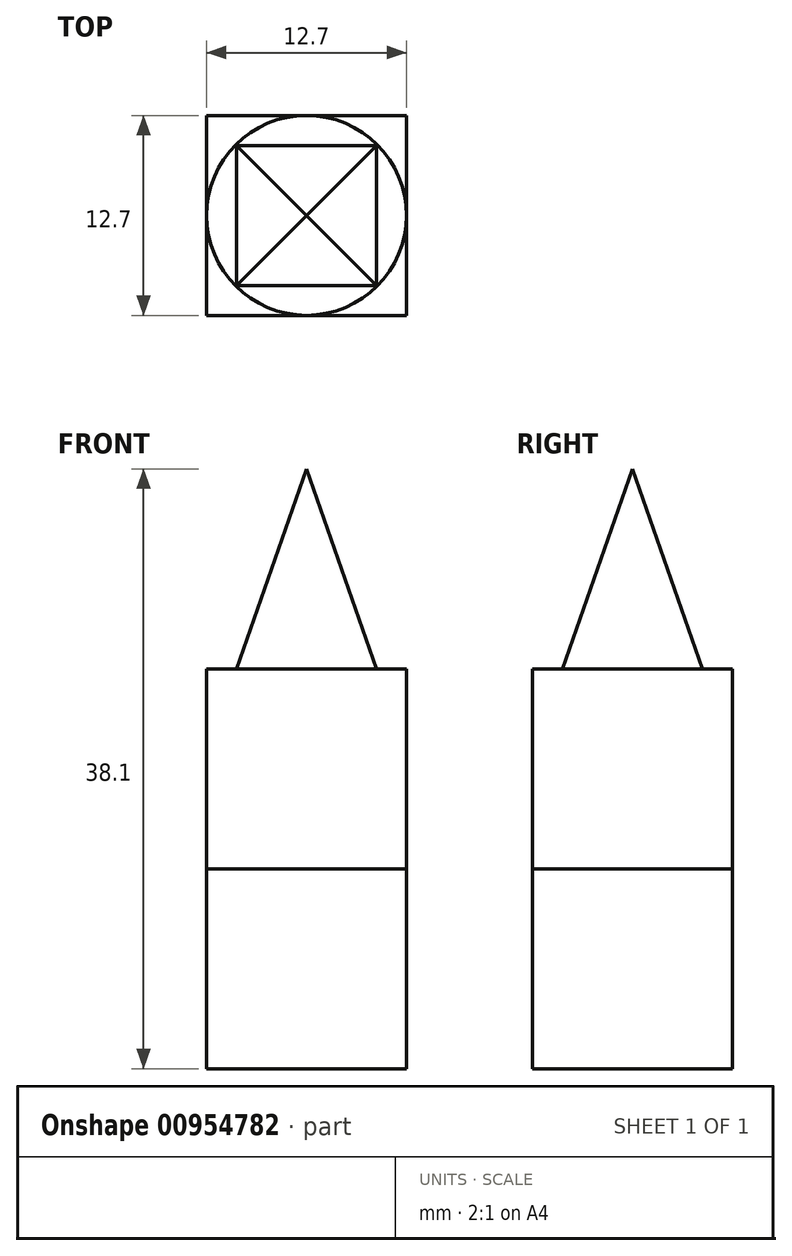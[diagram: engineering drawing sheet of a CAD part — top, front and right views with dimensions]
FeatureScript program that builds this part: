
annotation { "Feature Type Name" : "Feature", "Feature Type Description" : "" }
export const myFeature = defineFeature(function(context is Context, id is Id, definition is map)
    precondition{}
    {
        {
            var Q0;
            Q0=qCreatedBy(makeId("Top.planeOp"),FACE);
            var sketch = newSketch(context, id + "F0", { "sketchPlane" : qUnion([Q0])});
            skLineSegment(sketch, "E0.bottom", {"start": v(6.35, 6.35) * mm, "end": v(-6.35, 6.35) * mm});
            skLineSegment(sketch, "E0.top", {"start": v(6.35, -6.35) * mm, "end": v(-6.35, -6.35) * mm});
            skLineSegment(sketch, "E0.left", {"start": v(6.35, 6.35) * mm, "end": v(6.35, -6.35) * mm});
            skLineSegment(sketch, "E0.right", {"start": v(-6.35, 6.35) * mm, "end": v(-6.35, -6.35) * mm});
            skPoint(sketch, "E0.middle", {"position": v(0, 0) * mm});
            skSolve(sketch);
        }
        {
            var Q0;
            Q0 = qSketchRegion(id + "F0", true);
            extrude(context, id + "F1", {"entities" : qUnion([Q0]), "depth" : 12.7 * mm, "offsetDistance" : 25.4 * mm});
        }
        {
            var Q0;
            Q0=makeQuery(id+"F1.opExtrude","CAP_FACE",FACE,{"disambiguationData":[OSD([sQuery(id+"F0.wireOp",EDGE,"E0.bottom"),sQuery(id+"F0.wireOp",EDGE,"E0.top"),sQuery(id+"F0.wireOp",EDGE,"E0.left"),sQuery(id+"F0.wireOp",EDGE,"E0.right")])],"isStart":false});
            var sketch = newSketch(context, id + "F2", { "sketchPlane" : qUnion([Q0])});
            skCircle(sketch, "E1", {"center": v(0, 0) * mm, "radius": 6.35 * mm});
            skSolve(sketch);
        }
        {
            var Q0;
            Q0 = qSketchRegion(id + "F2", true);
            extrude(context, id + "F3", {"entities" : qUnion([Q0]), "operationType" : NewBodyOperationType.ADD, "depth" : 12.7 * mm, "offsetDistance" : 25.4 * mm});
        }
        {
            var Q0;
            Q0=makeQuery(id+"F3.opExtrude","CAP_FACE",FACE,{"disambiguationData":[OSD([sQuery(id+"F2.wireOp",EDGE,"E1")])],"isStart":false});
            var sketch = newSketch(context, id + "F4", { "sketchPlane" : qUnion([Q0])});
            skLineSegment(sketch, "E2.bottom", {"start": v(6.35, 6.35) * mm, "end": v(-6.35, 6.35) * mm});
            skLineSegment(sketch, "E2.top", {"start": v(6.35, -6.35) * mm, "end": v(-6.35, -6.35) * mm});
            skLineSegment(sketch, "E2.left", {"start": v(6.35, 6.35) * mm, "end": v(6.35, -6.35) * mm});
            skLineSegment(sketch, "E2.right", {"start": v(-6.35, 6.35) * mm, "end": v(-6.35, -6.35) * mm});
            skPoint(sketch, "E2.middle", {"position": v(0, 0) * mm});
            skSolve(sketch);
        }
        {
            var Q0;
            Q0 = qSketchRegion(id + "F4", true);
            extrude(context, id + "F5", {"entities" : qUnion([Q0]), "operationType" : NewBodyOperationType.ADD, "depth" : 12.7 * mm, "offsetDistance" : 25.4 * mm});
        }
        {
            var Q0;
            Q0=qCreatedBy(makeId("Front.planeOp"),FACE);
            var sketch = newSketch(context, id + "F6", { "sketchPlane" : qUnion([Q0])});
            skLineSegment(sketch, "E3.0", {"start": v(6.35, 25.4) * mm, "end": v(4.44, 25.4) * mm});
            skLineSegment(sketch, "E4.0", {"start": v(-4.44, 25.4) * mm, "end": v(-6.35, 25.4) * mm});
            skLineSegment(sketch, "E5.0", {"start": v(6.35, 38.1) * mm, "end": v(-6.35, 38.1) * mm});
            skLineSegment(sketch, "E6", {"start": v(-4.45, 25.4) * mm, "end": v(0, 38.1) * mm});
            skLineSegment(sketch, "E7", {"start": v(0, 38.1) * mm, "end": v(4.44, 25.4) * mm});
            skPoint(sketch, "E8.orphan", {"position": v(0, 25.4) * mm});
            skLineSegment(sketch, "E9.0", {"start": v(-6.35, 38.1) * mm, "end": v(-6.35, 25.4) * mm});
            skLineSegment(sketch, "E10.0", {"start": v(6.35, 38.1) * mm, "end": v(6.35, 25.4) * mm});
            skSolve(sketch);
        }
        {
            var Q0;
            Q0 = qSketchRegion(id + "F6", true);
            extrude(context, id + "F7", {"entities" : qUnion([Q0]), "operationType" : NewBodyOperationType.REMOVE, "endBound" : BoundingType.THROUGH_ALL, "oppositeDirection" : true, "depth" : 25.4 * mm, "offsetDistance" : 25.4 * mm, "hasSecondDirection" : true, "secondDirectionBound" : SecondDirectionBoundingType.THROUGH_ALL, "secondDirectionOppositeDirection" : false, "secondDirectionDepth" : 25.4 * mm});
        }
        {
            var Q0;
            Q0=qCreatedBy(makeId("Right.planeOp"),FACE);
            var sketch = newSketch(context, id + "F8", { "sketchPlane" : qUnion([Q0])});
            skLineSegment(sketch, "E11.0", {"start": v(-6.35, 38.1) * mm, "end": v(-6.35, 25.4) * mm});
            skLineSegment(sketch, "E12.0", {"start": v(6.35, 38.1) * mm, "end": v(6.35, 25.4) * mm});
            skPoint(sketch, "E13.0", {"position": v(0, 25.4) * mm});
            skLineSegment(sketch, "E14", {"start": v(4.45, 25.4) * mm, "end": v(0, 38.1) * mm});
            skLineSegment(sketch, "E15", {"start": v(0, 38.1) * mm, "end": v(-4.44, 25.4) * mm});
            skLineSegment(sketch, "E16", {"start": v(-6.35, 25.4) * mm, "end": v(-4.44, 25.4) * mm});
            skLineSegment(sketch, "E17", {"start": v(4.45, 25.4) * mm, "end": v(6.35, 25.4) * mm});
            skLineSegment(sketch, "E18", {"start": v(0, 38.1) * mm, "end": v(-6.35, 38.1) * mm});
            skLineSegment(sketch, "E19", {"start": v(0, 38.1) * mm, "end": v(6.35, 38.1) * mm});
            skSolve(sketch);
        }
        {
            var Q0;
            Q0 = qSketchRegion(id + "F8", true);
            extrude(context, id + "F9", {"entities" : qUnion([Q0]), "operationType" : NewBodyOperationType.REMOVE, "endBound" : BoundingType.THROUGH_ALL, "oppositeDirection" : true, "depth" : 25.4 * mm, "offsetDistance" : 25.4 * mm, "hasSecondDirection" : true, "secondDirectionBound" : SecondDirectionBoundingType.THROUGH_ALL, "secondDirectionOppositeDirection" : false, "secondDirectionDepth" : 25.4 * mm});
        }
    });
